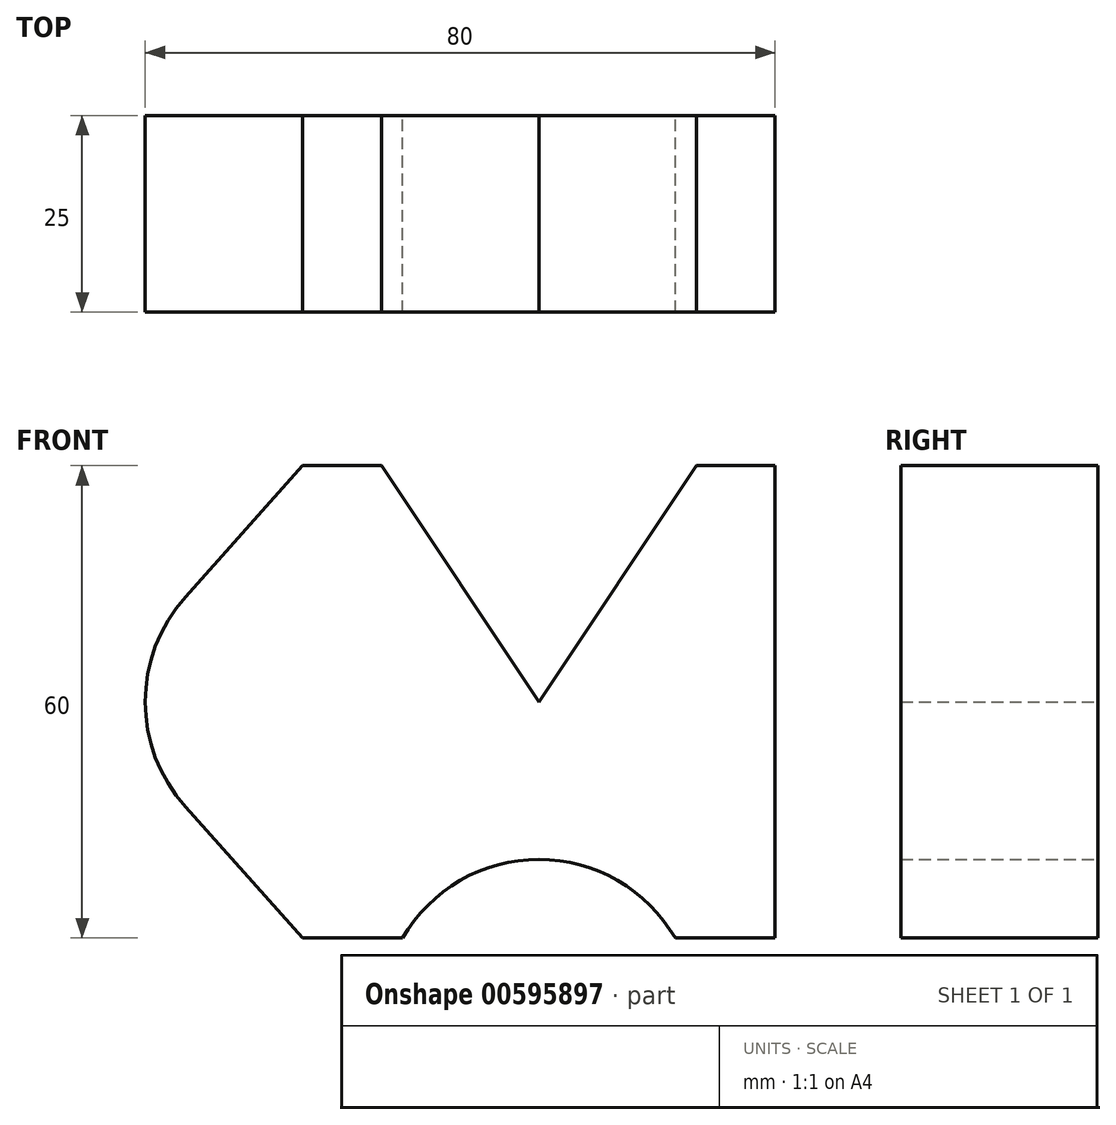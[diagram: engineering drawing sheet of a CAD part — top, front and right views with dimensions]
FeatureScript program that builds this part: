
annotation { "Feature Type Name" : "Feature", "Feature Type Description" : "" }
export const myFeature = defineFeature(function(context is Context, id is Id, definition is map)
    precondition{}
    {
        {
            var Q0;
            Q0=qCreatedBy(makeId("Front.planeOp"),FACE);
            var sketch = newSketch(context, id + "F0", { "sketchPlane" : qUnion([Q0])});
            skLineSegment(sketch, "E0.bottom", {"start": v(-30, 30) * mm, "end": v(-20, 30) * mm});
            skLineSegment(sketch, "E0.top", {"start": v(-30, -30) * mm, "end": v(-17.32, -30) * mm});
            skLineSegment(sketch, "E0.right", {"start": v(30, 30) * mm, "end": v(30, -30) * mm});
            skLineSegment(sketch, "E1", {"start": v(-20, 30) * mm, "end": v(0, 0) * mm});
            skLineSegment(sketch, "E2", {"start": v(0, 0) * mm, "end": v(20, 30) * mm});
            skArc(sketch, "E3", {"start": v(17.32, -30) * mm, "mid": v(0, -20) * mm, "end": v(-17.32, -30) * mm});
            skLineSegment(sketch, "E4.trimOffspring", {"start": v(17.32, -30) * mm, "end": v(30, -30) * mm});
            skLineSegment(sketch, "E5.trimOffspring", {"start": v(20, 30) * mm, "end": v(30, 30) * mm});
            skArc(sketch, "E6", {"start": v(-44.9, 13.33) * mm, "mid": v(-50, 0) * mm, "end": v(-44.9, -13.33) * mm});
            skLineSegment(sketch, "E7", {"start": v(-44.9, -13.33) * mm, "end": v(-30, -30) * mm});
            skLineSegment(sketch, "E8", {"start": v(-30, 30) * mm, "end": v(-44.9, 13.33) * mm});
            skSolve(sketch);
        }
        {
            var Q0;
            Q0 = qSketchRegion(id + "F0", true);
            extrude(context, id + "F1", {"entities" : qUnion([Q0]), "depth" : 25 * mm, "offsetDistance" : 25 * mm});
        }
    });
